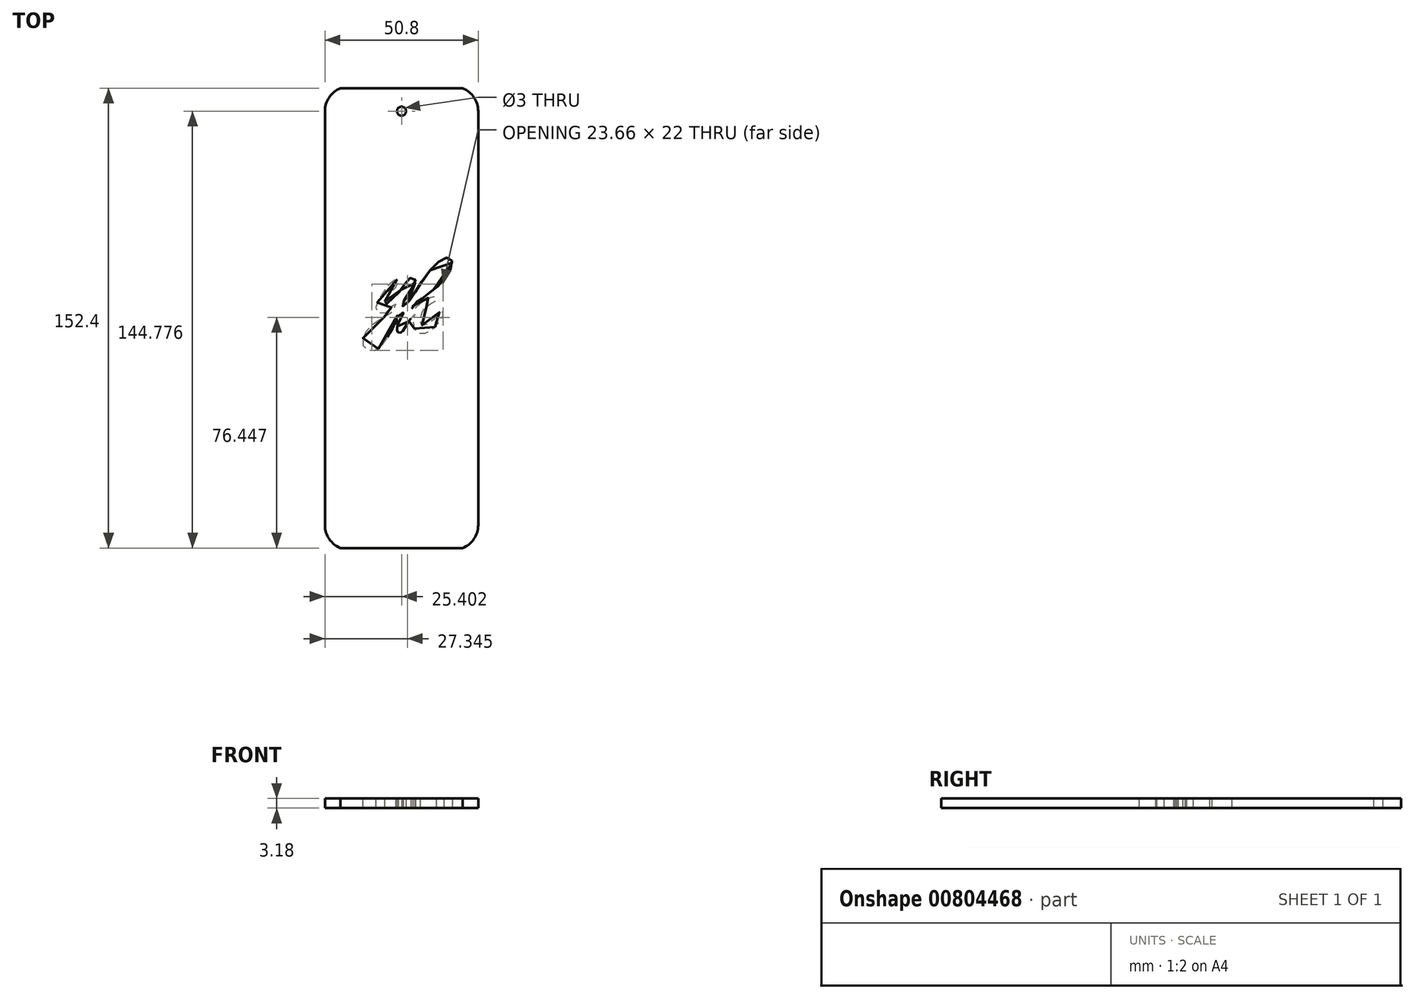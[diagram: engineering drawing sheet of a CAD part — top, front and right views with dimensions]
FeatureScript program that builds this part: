
annotation { "Feature Type Name" : "Feature", "Feature Type Description" : "" }
export const myFeature = defineFeature(function(context is Context, id is Id, definition is map)
    precondition{}
    {
        {
            var Q0;
            Q0=qCreatedBy(makeId("Top.planeOp"),FACE);
            var sketch = newSketch(context, id + "F0", { "sketchPlane" : qUnion([Q0])});
            skFitSpline(sketch, "E0", {"points": [v(-8.14, 37.34) * mm, v(-6.15, 40.5) * mm, v(-3.8, 42.93) * mm, v(-3.8, 44.2) * mm, v(-4.8, 44.42) * mm, v(-7.57, 41.93) * mm, v(-10, 38.09) * mm, v(-10.99, 35.95) * mm, v(-10.92, 34.24) * mm, v(-9, 33.24) * mm, v(-5.8, 35.45) * mm, v(-4.5, 36.8) * mm, v(-5.67, 33.8) * mm, v(-6.96, 32.94) * mm, v(-10.35, 30.92) * mm, v(-13.15, 28.73) * mm, v(-15.04, 26.17) * mm, v(-15.5, 23.63) * mm, v(-14.78, 21.82) * mm, v(-12.86, 21.05) * mm, v(-10.22, 21.66) * mm, v(-7.18, 25.58) * mm, v(-4.5, 31.05) * mm, v(-4.06, 32.57) * mm, v(-3.55, 32.57) * mm, v(-2, 33.69) * mm, v(-3.36, 30.65) * mm, v(-4.08, 28.14) * mm, v(-3.84, 27.18) * mm, v(-2.75, 27) * mm, v(-1.07, 29.26) * mm, v(0.96, 32.25) * mm, v(1.8, 33.08) * mm, v(1.28, 31.74) * mm, v(1.36, 29.13) * mm, v(2.37, 27.18) * mm, v(4.1, 26.6) * mm, v(6.37, 27.24) * mm, v(8.77, 29.18) * mm, v(10.67, 31.64) * mm, v(11.41, 33.1) * mm, v(11.17, 33.88) * mm, v(10.19, 33.85) * mm, v(9.01, 32.33) * mm, v(6.96, 30.44) * mm, v(5.47, 29.48) * mm, v(4.43, 29.34) * mm, v(3.63, 30.09) * mm, v(3.9, 32.65) * mm, v(4.5, 34.4) * mm, v(5.11, 35.34) * mm, v(7.29, 36.6) * mm, v(8.86, 37.59) * mm, v(8.65, 38.62) * mm, v(7.41, 38.89) * mm, v(5.07, 37.72) * mm, v(2.21, 35.48) * mm, v(0.58, 34) * mm, v(1.33, 36.09) * mm, v(2.84, 37.34) * mm, v(4.33, 38.29) * mm, v(7.46, 40.78) * mm, v(10.45, 43.42) * mm, v(13.47, 47.72) * mm, v(14.16, 50.44) * mm, v(13.23, 51.74) * mm, v(10.85, 51.18) * mm, v(7.17, 48.01) * mm, v(2.8, 41.93) * mm, v(0.61, 38.28) * mm, v(-2.07, 35.77) * mm, v(-2.58, 35.67) * mm, v(1.2, 42.24) * mm, v(2.05, 44.27) * mm, v(1.1, 45.25) * mm, v(-0.9, 44.05) * mm, v(-2.51, 41.45) * mm, v(-4.96, 38.88) * mm, v(-7.11, 36.88) * mm, v(-8.1, 36.37) * mm, v(-8.14, 37.34) * mm]});
            skFitSpline(sketch, "E1", {"points": [v(-6.97, 31.1) * mm, v(-8.56, 29.99) * mm, v(-11.05, 28.04) * mm, v(-12.68, 26.25) * mm, v(-13.2, 24.65) * mm, v(-12.87, 23.66) * mm, v(-11.63, 23.75) * mm, v(-9.8, 25.55) * mm, v(-7.86, 28.9) * mm, v(-6.97, 31.1) * mm]});
            skFitSpline(sketch, "E2", {"points": [v(3.53, 39.64) * mm, v(4.4, 41.2) * mm, v(7.36, 45.73) * mm, v(10.6, 48.86) * mm, v(11.54, 49.18) * mm, v(11.4, 47.61) * mm, v(9.43, 44.77) * mm, v(7.2, 42.4) * mm, v(3.53, 39.64) * mm]});
            skLineSegment(sketch, "E3.bottom", {"start": v(-27.98, 107.98) * mm, "end": v(22.82, 107.98) * mm});
            skLineSegment(sketch, "E3.top", {"start": v(-27.98, -44.42) * mm, "end": v(22.82, -44.42) * mm});
            skLineSegment(sketch, "E3.left", {"start": v(-27.98, 107.98) * mm, "end": v(-27.98, -44.42) * mm});
            skLineSegment(sketch, "E3.right", {"start": v(22.82, 107.98) * mm, "end": v(22.82, -44.42) * mm});
            skCircle(sketch, "E4", {"center": v(-2.58, 100.36) * mm, "radius": 1.5 * mm});
            skLineSegment(sketch, "E5", {"start": v(-2.58, 100.36) * mm, "end": v(22.82, 100.36) * mm, "construction": true});
            skLineSegment(sketch, "E6", {"start": v(-2.58, 100.36) * mm, "end": v(-27.98, 100.36) * mm, "construction": true});
            skArc(sketch, "E7", {"start": v(-22.83, 107.98) * mm, "mid": v(-26.57, 104.96) * mm, "end": v(-27.98, 100.36) * mm});
            skLineSegment(sketch, "E8", {"start": v(-27.98, 100.36) * mm, "end": v(-19.77, 100.36) * mm, "construction": true});
            skLineSegment(sketch, "E9", {"start": v(-2.58, 107.98) * mm, "end": v(-2.58, -44.42) * mm, "construction": true});
            skLineSegment(sketch, "E10", {"start": v(-27.98, 31.78) * mm, "end": v(22.82, 31.78) * mm, "construction": true});
            skArc(sketch, "E11.MirrorCS", {"start": v(17.67, 107.98) * mm, "mid": v(21.41, 104.96) * mm, "end": v(22.82, 100.36) * mm});
            skArc(sketch, "E12.MirrorCS", {"start": v(-22.83, -44.42) * mm, "mid": v(-26.57, -41.4) * mm, "end": v(-27.98, -36.8) * mm});
            skArc(sketch, "E13.MirrorCS", {"start": v(17.67, -44.42) * mm, "mid": v(21.41, -41.4) * mm, "end": v(22.82, -36.8) * mm});
            skSolve(sketch);
        }
        {
            var Q0;
            Q0=makeQuery(id+"F0.imprint","IMPRINT",FACE,{"disambiguationData":[TD([[makeQuery(id+"F0.imprint","IMPRINT",EDGE,{"derivedFrom":sQuery(id+"F0.wireOp",EDGE,"E0")}),-1.0]])]});
            extrude(context, id + "F1", {"entities" : qUnion([Q0]), "depth" : 3.17 * mm, "offsetDistance" : 25.4 * mm});
        }
    });
